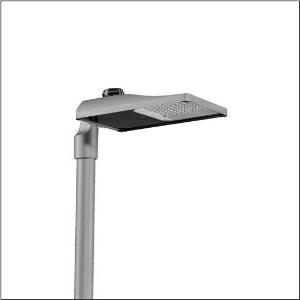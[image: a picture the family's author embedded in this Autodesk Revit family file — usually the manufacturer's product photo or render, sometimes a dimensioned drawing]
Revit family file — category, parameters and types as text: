
# Revit family: streetlight_sl_31_midi___pl52_5xh7h75n08ma_9a16
name_source: partatom
category: Lighting Fixtures
units: mm (PartAtom-declared; Revit-internal decimal feet)

## family parameters
Cut with Voids When Loaded = No
Host = Face
Light Source = No
Part Type = Normal
Room Calculation Point = No
Round Connector Dimension = Use Diameter
Shared = No

## types (1)
- --- (1 x LED, 15810 lm, 145.3 W, 2200K)
    Apparent Load = 145 VA
    CIE Flux Codes = 27 59 98 100 100
    Color Rendering = 70
    Color Temperature = 2200K
    Default Elevation = 1800 mm
    Description = Streetlight SL 31 midi NEMA (7pin), Desk-Remote mast luminaire for post-top, side-entry; light control with lens of PMMA; light distribution: PL52, direct asymmetric distribution, for standard-compliant lighting for roads and squares; LED: luminous flux: 15.810lm, light colour: 722, colour temperature: 2200K; luminous efficacy: 108,8lm/W; control: pre-setting: linear dimming characteristic, flexible luminous flux parameterisation, time-dependent luminous flux control, constant luminous flux control, intelligent temperature release in ECG and LED module, overheat protection; luminaire housing, of diecast aluminium, Siteco® metallic grey (DB 702S), corrosivity category C5 high according to DIN EN ISO 12944; cover of toughened safety glass, transparent, opened without tools; mast flange of diecast aluminium, Siteco® metallic grey (DB 702S), spigot size: 76/60mm, mast flange included unmounted; with cable H07RN-F 3x 1.5mm², cable length: 12,5m, connection cable pre-assembled; mains connection: 220..240V, AC, 50/60Hz; power consumption (at start of service life): 145,3W / (at end of service life): 161,8W / (with reduced operation 50%): 61,1W; protection rating (complete): IP66; insulation class (complete): insulation class I (protective earthing); impact resistance: IK10; certification: CE, ENEC, ENEC+, VDE, UKCA; permissible operating ambient temperature for outdoor applications: -40..+50°C; packaging unit: 1 piece

Light Distribution: PL52
    Height = 79 mm
    Lamp = 1 x LED
    Lamp Light Flux = 15810 lm
    Lamp Power = 145.3 W
    Lamp count = 1
    Length = 577 mm
    Luminous efficacy = 109 lm/W
    Manufacturer = Siteco
    ModVariant = No
    Model = 5XH7H75N08MA
    Number of Poles = 1
    OnlyDefault = Yes
    Power Factor = 1
    Product Name = Streetlight SL 31 midi | PL52
    Product group = mast luminaire | pylon top
    ProductGroupID = 6100
    Protection Class = Protection class I
    Protection Degree = IP 66
    RLX_Detail_Level = 1
    RLX_Emergency_Light_Flux = 0 lm
    RLX_Emergency_Type = 0
    RLX_Emergency_Type_DB = No
    RlxData = <blob elided: 52569 chars, md5=0222b3b0>
    Socket = socket
    Standby Power = 0 W
    System Light Flux = 15810 lm
    System Power = 145 W
    Type Comments = factory setting: luminous flux: 100 % | dim-lin: 254 | 747 mA
    Type Image = l_1300282.jpg
    URL = http://relux.com
    VarID = @adj_057646
    Voltage = 0 V
    Weight = 0.00 kg
    Width = 362 mm

## geometry (parser evidence)
native form markers: Blend x4, Sweep x10
no freeform markers — native parametric forms only
